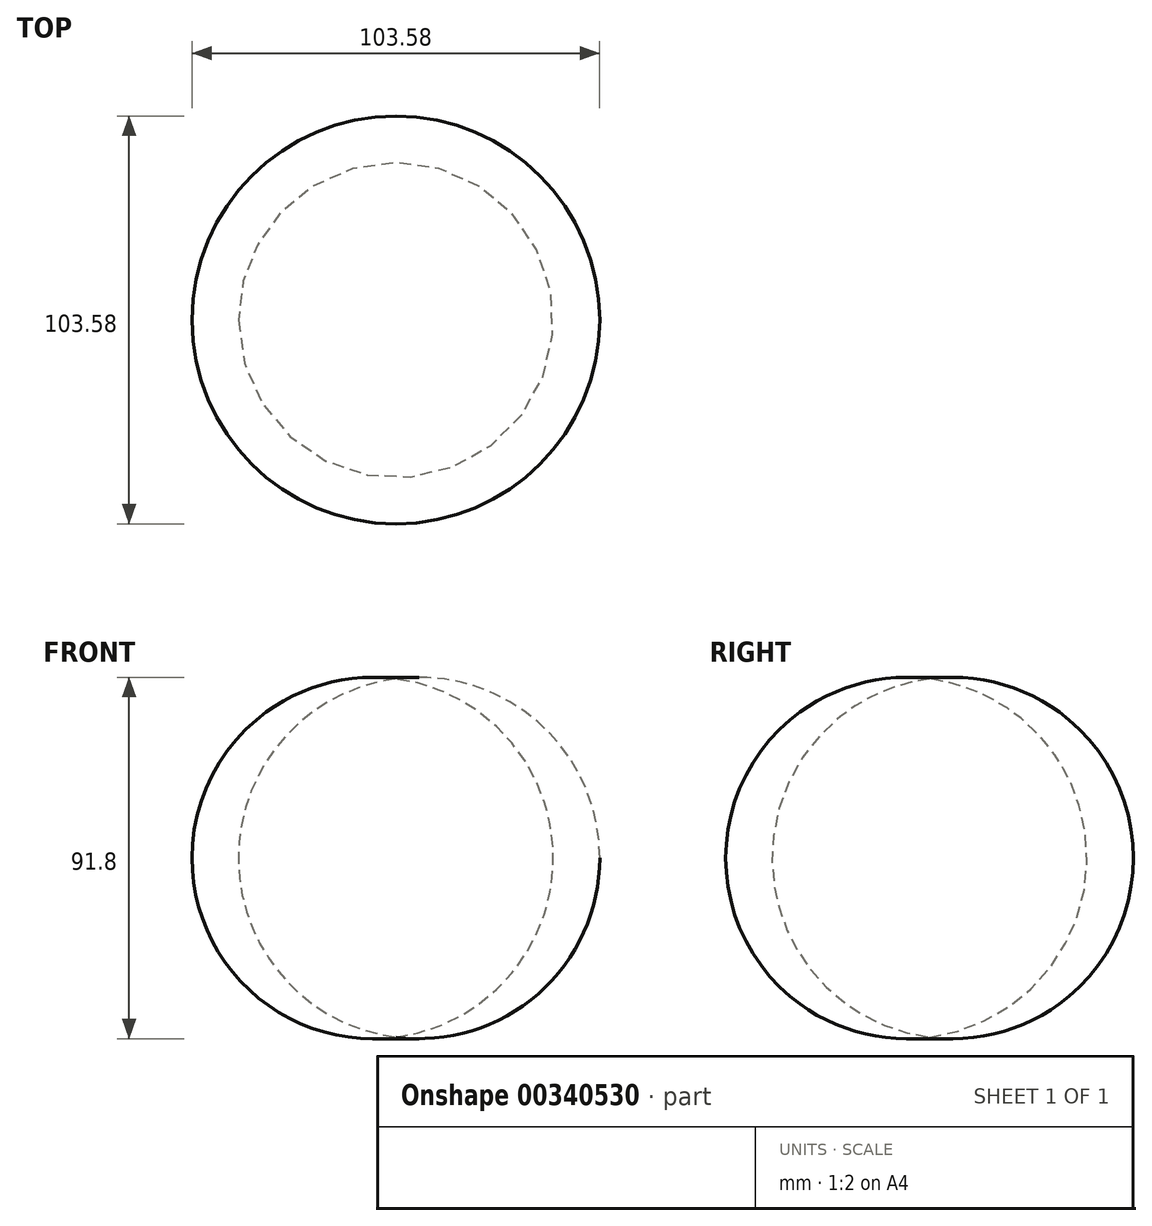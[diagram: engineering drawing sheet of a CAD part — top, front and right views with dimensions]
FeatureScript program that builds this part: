
annotation { "Feature Type Name" : "Feature", "Feature Type Description" : "" }
export const myFeature = defineFeature(function(context is Context, id is Id, definition is map)
    precondition{}
    {
        {
            var Q0;
            Q0=qCreatedBy(makeId("Front.planeOp"),FACE);
            var sketch = newSketch(context, id + "F0", { "sketchPlane" : qUnion([Q0])});
            skLineSegment(sketch, "E0", {"start": v(0, 45.5) * mm, "end": v(0, -45.53) * mm});
            skArc(sketch, "E1", {"start": v(0, -45.53) * mm, "mid": v(40, -0.01) * mm, "end": v(0, 45.5) * mm});
            skSolve(sketch);
        }
        {
            var Q0;
            Q0=makeQuery(id+"F0.imprint","IMPRINT",FACE,{"disambiguationData":[TD([[makeQuery(id+"F0.imprint","IMPRINT",EDGE,{"derivedFrom":sQuery(id+"F0.wireOp",EDGE,"E0")}),1.0]])]});
            var Q1;
            Q1=sQuery(id+"F0.wireOp",EDGE,"E0");
            revolve(context, id + "F1", {"entities" : qUnion([Q0]), "axis" : qUnion([Q1]), "revolveType" : RevolveType.FULL});
        }
    });
